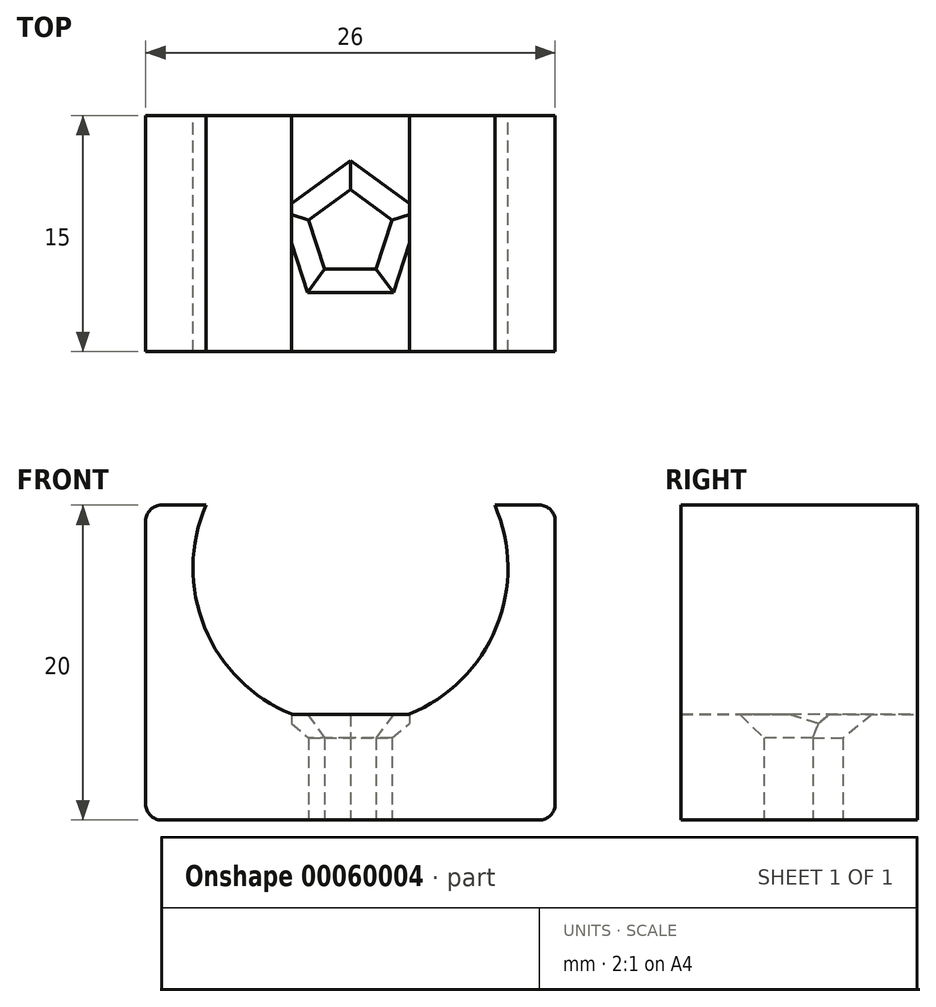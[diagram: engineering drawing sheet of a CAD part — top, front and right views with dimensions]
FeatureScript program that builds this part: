
annotation { "Feature Type Name" : "Feature", "Feature Type Description" : "" }
export const myFeature = defineFeature(function(context is Context, id is Id, definition is map)
    precondition{}
    {
        {
            var Q0;
            Q0=qCreatedBy(makeId("Front.planeOp"),FACE);
            var sketch = newSketch(context, id + "F0", { "sketchPlane" : qUnion([Q0])});
            skLineSegment(sketch, "E0", {"start": v(-15.24, 21.35) * mm, "end": v(-15.24, 1.35) * mm});
            skLineSegment(sketch, "E1", {"start": v(-15.24, 1.35) * mm, "end": v(10.76, 1.35) * mm});
            skLineSegment(sketch, "E2", {"start": v(10.76, 1.35) * mm, "end": v(10.76, 21.35) * mm});
            skLineSegment(sketch, "E3", {"start": v(10.76, 21.35) * mm, "end": v(6.92, 21.35) * mm});
            skLineSegment(sketch, "E4", {"start": v(-15.24, 21.35) * mm, "end": v(-11.4, 21.35) * mm});
            skArc(sketch, "E5", {"start": v(-11.4, 21.35) * mm, "mid": v(-2.24, 7.35) * mm, "end": v(6.92, 21.35) * mm});
            skSolve(sketch);
        }
        {
            var Q0;
            Q0=makeQuery(id+"F0.imprint","IMPRINT",FACE,{"disambiguationData":[TD([[makeQuery(id+"F0.imprint","IMPRINT",EDGE,{"derivedFrom":sQuery(id+"F0.wireOp",EDGE,"E0")}),1.0]])]});
            var Q1;
            Q1 = qSketchRegion(id + "F2", true);
            extrude(context, id + "F1", {"entities" : qUnion([Q0, Q1]), "depth" : 15 * mm, "offsetDistance" : 25 * mm});
        }
        {
            var Q0;
            Q0=makeQuery(id+"F1.opExtrude","SWEPT_FACE",FACE,{"disambiguationData":[OSD([sQuery(id+"F0.wireOp",EDGE,"E1")])]});
            var sketch = newSketch(context, id + "F2", { "sketchPlane" : qUnion([Q0])});
            skLineSegment(sketch, "E6.0", {"start": v(-3.88, 9.75) * mm, "end": v(-0.6, 9.75) * mm});
            skLineSegment(sketch, "E6.1", {"start": v(-0.6, 9.75) * mm, "end": v(0.4, 6.64) * mm});
            skLineSegment(sketch, "E6.2", {"start": v(0.4, 6.64) * mm, "end": v(-2.24, 4.72) * mm});
            skLineSegment(sketch, "E6.3", {"start": v(-2.24, 4.72) * mm, "end": v(-4.89, 6.64) * mm});
            skLineSegment(sketch, "E6.4", {"start": v(-4.89, 6.64) * mm, "end": v(-3.88, 9.75) * mm});
            skPoint(sketch, "E6.0.midPoint", {"position": v(-2.24, 9.75) * mm});
            skPoint(sketch, "E7.center.orphan", {"position": v(-2.24, 7.5) * mm});
            skSolve(sketch);
        }
        {
            var Q0;
            Q0=makeQuery(id+"F2.imprint","IMPRINT",FACE,{"disambiguationData":[TD([[makeQuery(id+"F2.imprint","IMPRINT",EDGE,{"derivedFrom":sQuery(id+"F2.wireOp",EDGE,"E6.0")}),-1.0]])]});
            extrude(context, id + "F3", {"entities" : qUnion([Q0]), "operationType" : NewBodyOperationType.REMOVE, "oppositeDirection" : true, "offsetDistance" : 25 * mm, "depth" : 8 * mm});
        }
        {
            var Q0;
            Q0=makeQuery(id+"F1.opExtrude","SWEPT_FACE",FACE,{"disambiguationData":[OSD([sQuery(id+"F0.wireOp",EDGE,"E1")])]});
            var sketch = newSketch(context, id + "F4", { "sketchPlane" : qUnion([Q0])});
            skLineSegment(sketch, "E8.bottom", {"start": v(1.5, 0) * mm, "end": v(-5.99, 0) * mm});
            skLineSegment(sketch, "E8.top", {"start": v(1.5, 15) * mm, "end": v(-5.99, 15) * mm});
            skLineSegment(sketch, "E8.left", {"start": v(-5.99, 15) * mm, "end": v(-5.99, 0) * mm});
            skLineSegment(sketch, "E8.right", {"start": v(1.5, 15) * mm, "end": v(1.5, 0) * mm});
            skSolve(sketch);
        }
        {
            var Q0;
            Q0=makeQuery(id+"F4.imprint","IMPRINT",FACE,{"disambiguationData":[TD([[makeQuery(id+"F4.imprint","IMPRINT",EDGE,{"derivedFrom":sQuery(id+"F4.wireOp",EDGE,"E8.bottom")}),1.0]])]});
            extrude(context, id + "F5", {"entities" : qUnion([Q0]), "operationType" : NewBodyOperationType.REMOVE, "oppositeDirection" : true, "depth" : 8 * mm, "offsetDistance" : 25 * mm});
        }
        {
            var Q0;
            Q0=makeQuery(id+"F4.imprint","IMPRINT",FACE,{"disambiguationData":[TD([[makeQuery(id+"F4.imprint","IMPRINT",EDGE,{"derivedFrom":sQuery(id+"F4.wireOp",EDGE,"E8.bottom")}),1.0]])]});
            extrude(context, id + "F6", {"entities" : qUnion([Q0]), "operationType" : NewBodyOperationType.ADD, "oppositeDirection" : true, "depth" : 6.7 * mm, "offsetDistance" : 25 * mm});
        }
        {
            var Q0;
            Q0=makeQuery(id+"F6.opExtrude","CAP_EDGE",EDGE,{"disambiguationData":[OSD([sQuery(id+"F2.wireOp",EDGE,"E6.3")])],"isStart":false});
            var Q1;
            Q1=makeQuery(id+"F6.opExtrude","CAP_EDGE",EDGE,{"disambiguationData":[OSD([sQuery(id+"F2.wireOp",EDGE,"E6.2")])],"isStart":false});
            var Q2;
            Q2=makeQuery(id+"F6.opExtrude","CAP_EDGE",EDGE,{"disambiguationData":[OSD([sQuery(id+"F2.wireOp",EDGE,"E6.1")])],"isStart":false});
            var Q3;
            Q3=makeQuery(id+"F6.opExtrude","CAP_EDGE",EDGE,{"disambiguationData":[OSD([sQuery(id+"F2.wireOp",EDGE,"E6.0")])],"isStart":false});
            var Q4;
            Q4=makeQuery(id+"F6.opExtrude","CAP_EDGE",EDGE,{"disambiguationData":[OSD([sQuery(id+"F2.wireOp",EDGE,"E6.4")])],"isStart":false});
            chamfer(context, id + "F7", {"entities" : qUnion([Q0, Q1, Q2, Q3, Q4]), "width" : 1.5 * mm, "tangentPropagation" : true});
        }
        {
            var Q0;
            Q0=makeQuery(id+"F1.opExtrude","SWEPT_EDGE",EDGE,{"disambiguationData":[OSD([sQuery(id+"F0.wireOp",EDGE,"E0"),sQuery(id+"F0.wireOp",EDGE,"E4")])]});
            var Q1;
            Q1=makeQuery(id+"F1.opExtrude","SWEPT_EDGE",EDGE,{"disambiguationData":[OSD([sQuery(id+"F0.wireOp",EDGE,"E2"),sQuery(id+"F0.wireOp",EDGE,"E3")])]});
            var Q2;
            Q2=makeQuery(id+"F1.opExtrude","SWEPT_EDGE",EDGE,{"disambiguationData":[OSD([sQuery(id+"F0.wireOp",EDGE,"E1"),sQuery(id+"F0.wireOp",EDGE,"E2")])]});
            var Q3;
            Q3=makeQuery(id+"F1.opExtrude","SWEPT_EDGE",EDGE,{"disambiguationData":[OSD([sQuery(id+"F0.wireOp",EDGE,"E0"),sQuery(id+"F0.wireOp",EDGE,"E1")])]});
            fillet(context, id + "F8", {"entities" : qUnion([Q0, Q1, Q2, Q3]), "radius" : 1 * mm, "tangentPropagation" : true, "allowEdgeOverflow" : false});
        }
    });
